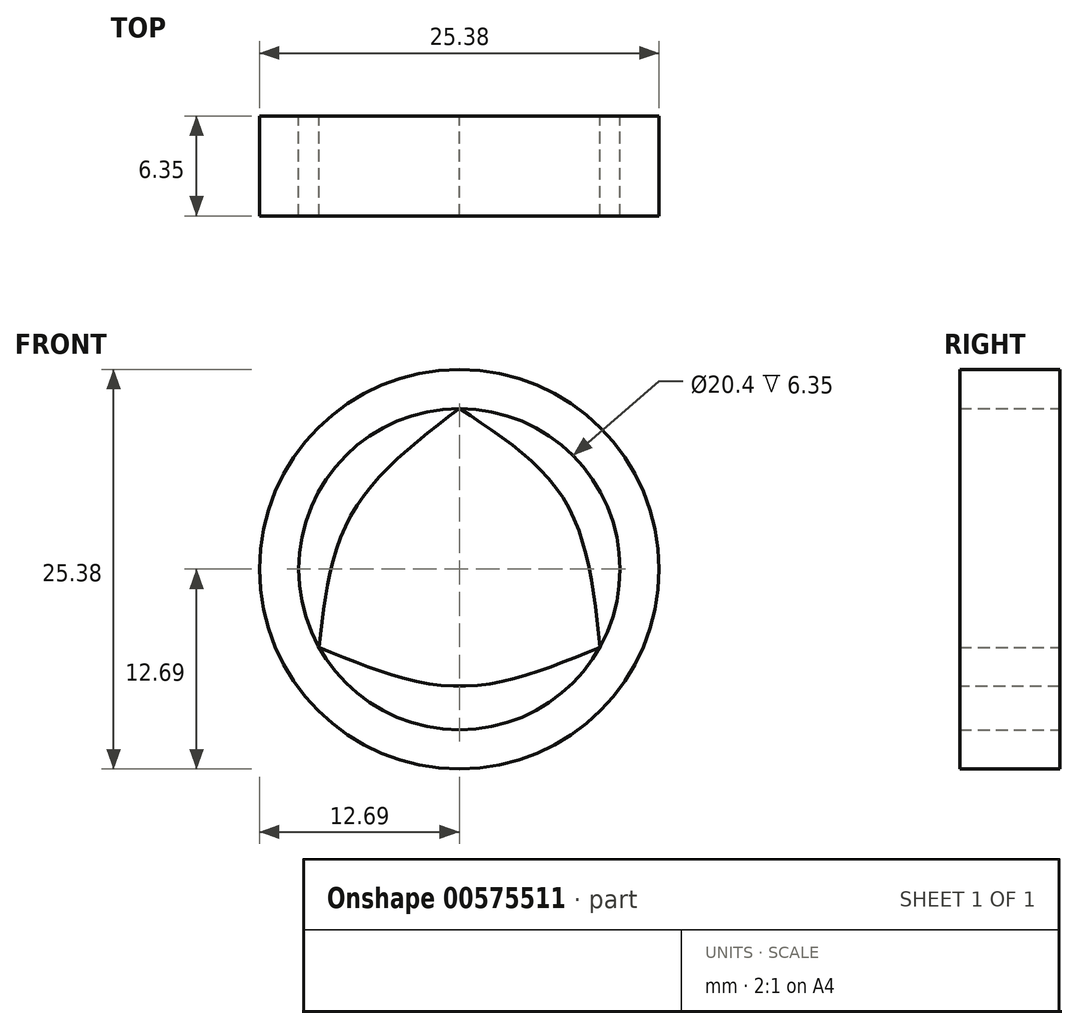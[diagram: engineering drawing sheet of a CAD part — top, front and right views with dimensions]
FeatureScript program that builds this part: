
annotation { "Feature Type Name" : "Feature", "Feature Type Description" : "" }
export const myFeature = defineFeature(function(context is Context, id is Id, definition is map)
    precondition{}
    {
        {
            var Q0;
            Q0=qCreatedBy(makeId("Front.planeOp"),FACE);
            var sketch = newSketch(context, id + "F0", { "sketchPlane" : qUnion([Q0])});
            skCircle(sketch, "E0", {"center": v(0, 0) * mm, "radius": 12.7 * mm});
            skCircle(sketch, "E1", {"center": v(0, 0) * mm, "radius": 10.2 * mm});
            skLineSegment(sketch, "E2", {"start": v(0, 10.2) * mm, "end": v(8.92, -4.96) * mm});
            skLineSegment(sketch, "E3", {"start": v(8.92, -4.96) * mm, "end": v(-8.92, -4.96) * mm});
            skLineSegment(sketch, "E4", {"start": v(0, 10.2) * mm, "end": v(-8.92, -4.96) * mm});
            skFitSpline(sketch, "E5", {"points": [v(-8.92, -4.96) * mm, v(-6.8, 3.57) * mm, v(0, 10.2) * mm], "startDerivative": vector(2.12, 18.46) * mm, "endDerivative": vector(15.63, 11.9) * mm});
            skFitSpline(sketch, "E6", {"points": [v(0, 10.2) * mm, v(6.69, 4.36) * mm, v(8.92, -4.96) * mm], "startDerivative": vector(15.9, -10.34) * mm, "endDerivative": vector(2.02, -19.91) * mm});
            skFitSpline(sketch, "E7", {"points": [v(8.92, -4.96) * mm, v(0, -7.44) * mm, v(-8.92, -4.96) * mm], "startDerivative": vector(-17.84, -7.44) * mm, "endDerivative": vector(-17.84, 7.44) * mm});
            skSolve(sketch);
        }
        {
            var Q0;
            Q0=makeQuery(id+"F0.imprint","IMPRINT",FACE,{"disambiguationData":[TD([[makeQuery(id+"F0.imprint","IMPRINT",EDGE,{"derivedFrom":sQuery(id+"F0.wireOp",EDGE,"E0")}),1.0]])]});
            var Q1;
            Q1=makeQuery(id+"F0.imprint","IMPRINT",FACE,{"disambiguationData":[TD([[makeQuery(id+"F0.imprint","IMPRINT",EDGE,{"derivedFrom":sQuery(id+"F0.wireOp",EDGE,"E2")}),-1.0]])]});
            var Q2;
            Q2=makeQuery(id+"F0.imprint","IMPRINT",FACE,{"disambiguationData":[TD([[makeQuery(id+"F0.imprint","IMPRINT",EDGE,{"derivedFrom":sQuery(id+"F0.wireOp",EDGE,"E2")}),1.0]])]});
            var Q3;
            Q3=makeQuery(id+"F0.imprint","IMPRINT",FACE,{"disambiguationData":[TD([[makeQuery(id+"F0.imprint","IMPRINT",EDGE,{"derivedFrom":sQuery(id+"F0.wireOp",EDGE,"E3")}),1.0]])]});
            var Q4;
            Q4=makeQuery(id+"F0.imprint","IMPRINT",FACE,{"disambiguationData":[TD([[makeQuery(id+"F0.imprint","IMPRINT",EDGE,{"derivedFrom":sQuery(id+"F0.wireOp",EDGE,"E4")}),-1.0]])]});
            extrude(context, id + "F1", {"entities" : qUnion([Q0, Q1, Q2, Q3, Q4]), "depth" : 6.35 * mm, "offsetDistance" : 25.4 * mm});
        }
    });
